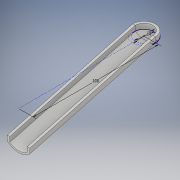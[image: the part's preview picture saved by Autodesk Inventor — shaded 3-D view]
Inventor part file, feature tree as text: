
AUTODESK INVENTOR PART (.ipt)
format: ipt  version: 2019 (Build 230136000, 136)  size: 153,088 bytes
history: native  units: mm
features: sketch x6, other x3, extrude x2, mirror x1, sweep x1
ambient origin geometry x8: Origin, YZ Plane, XZ Plane, XY Plane, X Axis, Y Axis, Z Axis, Center Point
bodies: Solide1 (feature_tree)
feature tree (13):
  sketch  "Esquisse1"
  other  "Plan de construction1"
  extrude  "Extrusion1"  Depth=100.0mm
  mirror  "Symétrie1"
  other  "Plan de construction2"
  extrude  "Extrusion2"  Depth=14.0mm
  sweep  "Balayage2"
  other  "Révolution1"
  sketch  "Esquisse3"
  sketch  "Esquisse4"
  sketch  "Esquisse5"
  sketch  "Esquisse 3D1"
  sketch  "Esquisse6"
